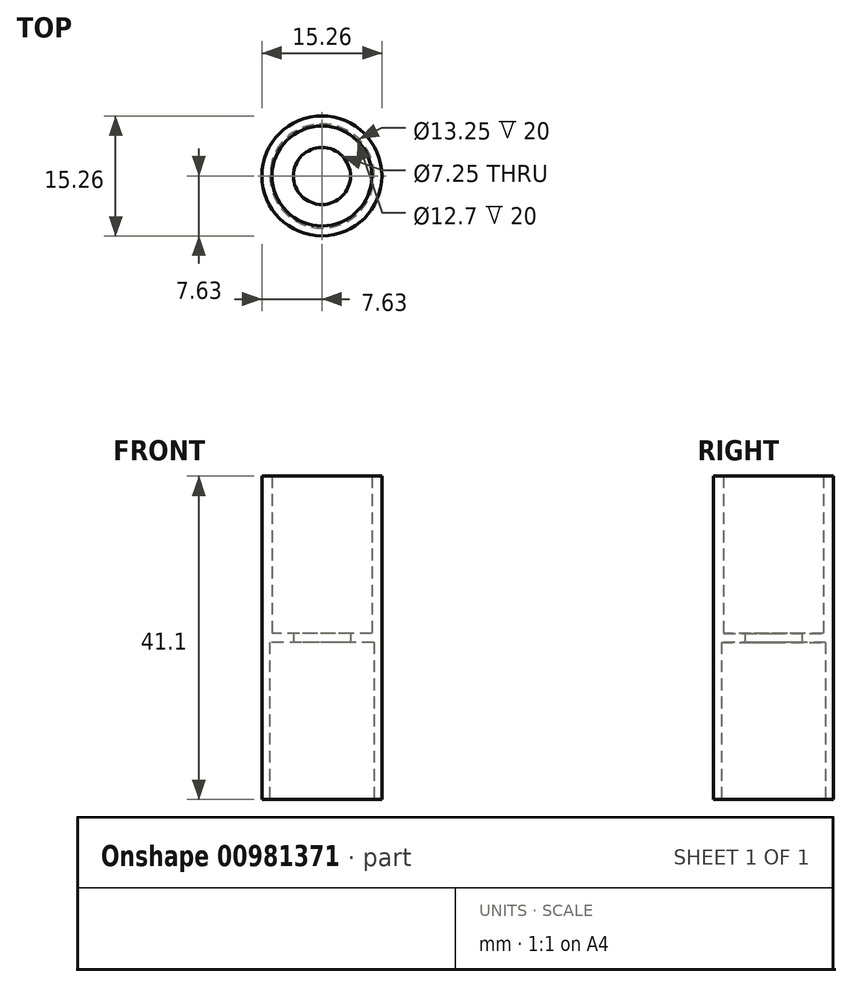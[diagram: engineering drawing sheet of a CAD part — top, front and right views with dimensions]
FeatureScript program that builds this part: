
annotation { "Feature Type Name" : "Feature", "Feature Type Description" : "" }
export const myFeature = defineFeature(function(context is Context, id is Id, definition is map)
    precondition{}
    {
        {
            var Q0;
            Q0=qCreatedBy(makeId("Top.planeOp"),FACE);
            var sketch = newSketch(context, id + "F0", { "sketchPlane" : qUnion([Q0])});
            skCircle(sketch, "E0", {"center": v(0, 0) * mm, "radius": 6.63 * mm});
            skCircle(sketch, "E1", {"center": v(0, 0) * mm, "radius": 7.62 * mm});
            skSolve(sketch);
        }
        {
            var Q0;
            Q0=makeQuery(id+"F0.imprint","IMPRINT",FACE,{"disambiguationData":[TD([[makeQuery(id+"F0.imprint","IMPRINT",EDGE,{"derivedFrom":sQuery(id+"F0.wireOp",EDGE,"E0")}),-1.0]])]});
            extrude(context, id + "F1", {"entities" : qUnion([Q0]), "depth" : 20 * mm, "offsetDistance" : 25 * mm});
        }
        {
            var Q0;
            Q0=makeQuery(id+"F1.opExtrude","CAP_FACE",FACE,{"disambiguationData":[OSD([sQuery(id+"F0.wireOp",EDGE,"E0"),sQuery(id+"F0.wireOp",EDGE,"E1")])],"isStart":false});
            var sketch = newSketch(context, id + "F2", { "sketchPlane" : qUnion([Q0])});
            skCircle(sketch, "E2", {"center": v(0, 0) * mm, "radius": 3.63 * mm});
            skCircle(sketch, "E3.0", {"center": v(0, 0) * mm, "radius": 7.62 * mm});
            skCircle(sketch, "E4.0", {"center": v(0, 0) * mm, "radius": 6.63 * mm});
            skSolve(sketch);
        }
        {
            var Q0;
            Q0=makeQuery(id+"F2.imprint","IMPRINT",FACE,{"disambiguationData":[TD([[makeQuery(id+"F2.imprint","IMPRINT",EDGE,{"derivedFrom":sQuery(id+"F2.wireOp",EDGE,"E2")}),-1.0]])]});
            var Q1;
            Q1=makeQuery(id+"F2.imprint","IMPRINT",FACE,{"disambiguationData":[TD([[makeQuery(id+"F2.imprint","IMPRINT",EDGE,{"derivedFrom":sQuery(id+"F2.wireOp",EDGE,"E3.0")}),1.0]])]});
            extrude(context, id + "F3", {"entities" : qUnion([Q0, Q1]), "operationType" : NewBodyOperationType.ADD, "depth" : 1.1 * mm, "offsetDistance" : 25 * mm});
        }
        {
            var Q0;
            Q0=makeQuery(id+"F3.opExtrude","CAP_FACE",FACE,{"disambiguationData":[OSD([sQuery(id+"F2.wireOp",EDGE,"E2"),sQuery(id+"F2.wireOp",EDGE,"E3.0")])],"isStart":false});
            var sketch = newSketch(context, id + "F4", { "sketchPlane" : qUnion([Q0])});
            skCircle(sketch, "E5", {"center": v(0, 0) * mm, "radius": 6.35 * mm});
            skSolve(sketch);
        }
        {
            var Q0;
            Q0=makeQuery(id+"F4.imprint","IMPRINT",FACE,{"disambiguationData":[TD([[makeQuery(id+"F4.imprint","IMPRINT",EDGE,{"derivedFrom":sQuery(id+"F4.wireOp",EDGE,"E5")}),-1.0]])]});
            extrude(context, id + "F5", {"entities" : qUnion([Q0]), "operationType" : NewBodyOperationType.ADD, "depth" : 20 * mm, "offsetDistance" : 25 * mm});
        }
    });
